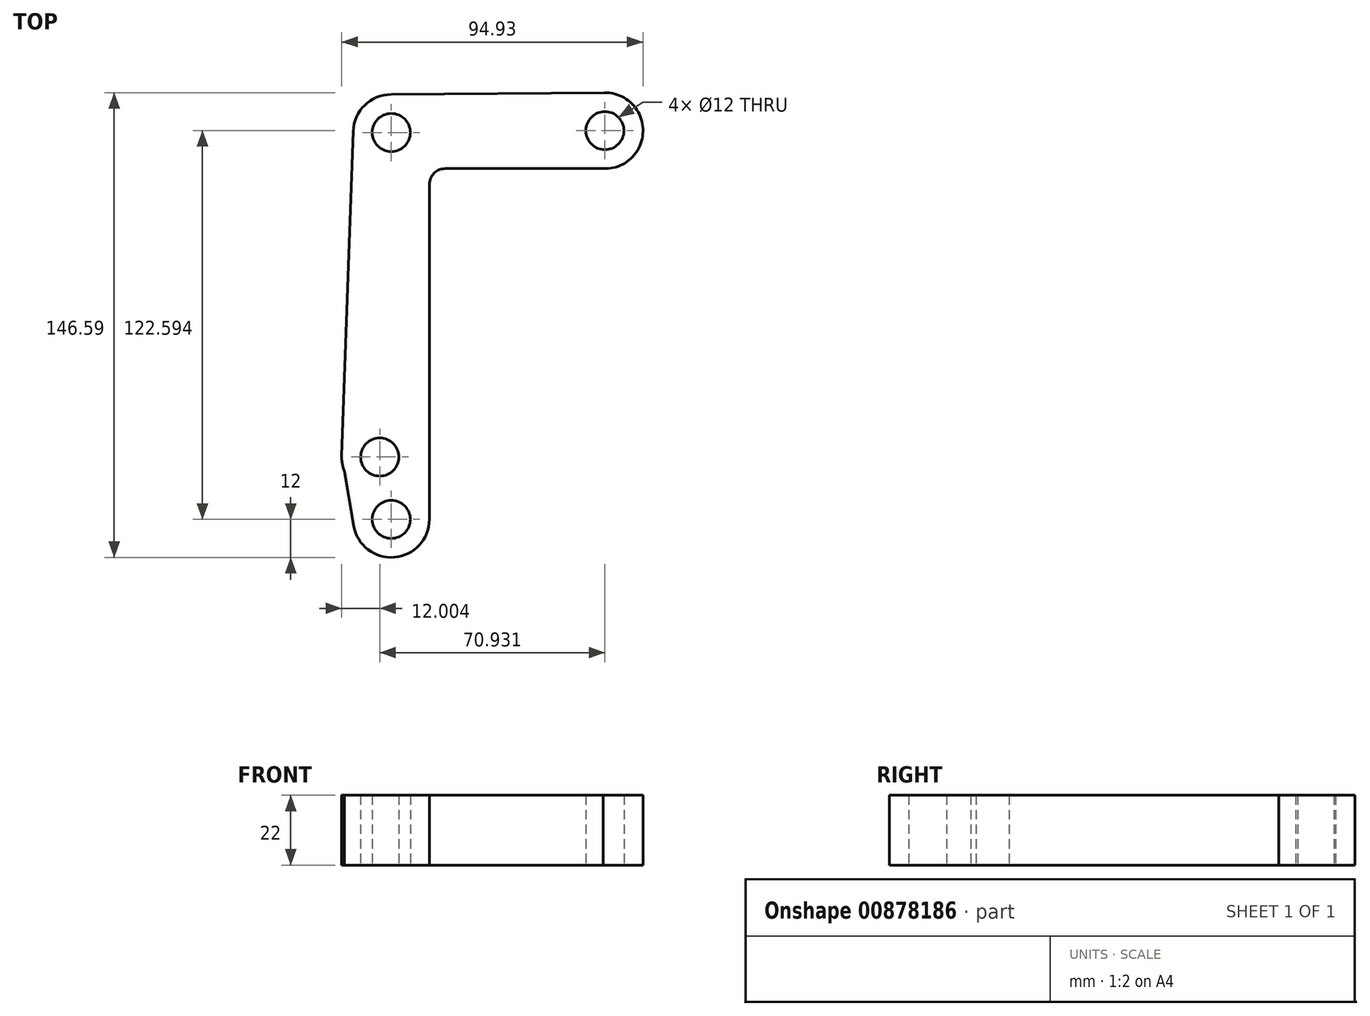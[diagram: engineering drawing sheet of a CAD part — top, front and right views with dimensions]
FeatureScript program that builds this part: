
annotation { "Feature Type Name" : "Feature", "Feature Type Description" : "" }
export const myFeature = defineFeature(function(context is Context, id is Id, definition is map)
    precondition{}
    {
        {
            var Q0;
            Q0=qCreatedBy(makeId("Top.planeOp"),FACE);
            var sketch = newSketch(context, id + "F0", { "sketchPlane" : qUnion([Q0])});
            skCircle(sketch, "E0", {"center": v(0, 0) * mm, "radius": 162 * mm, "construction": true});
            skLineSegment(sketch, "E1", {"start": v(-162, 0) * mm, "end": v(-116, 0) * mm, "construction": true});
            skLineSegment(sketch, "E2", {"start": v(-116, 0) * mm, "end": v(-70, 0) * mm, "construction": true});
            skLineSegment(sketch, "E3", {"start": v(-46.54, 61) * mm, "end": v(-46.54, -61) * mm, "construction": true});
            skCircle(sketch, "E4", {"center": v(0, 0) * mm, "radius": 65 * mm, "construction": true});
            skLineSegment(sketch, "E5", {"start": v(-50.17, -41.33) * mm, "end": v(20.76, 61.6) * mm, "construction": true});
            skCircle(sketch, "E6", {"center": v(20.76, 61.6) * mm, "radius": 6 * mm});
            skCircle(sketch, "E7", {"center": v(-50.17, -41.33) * mm, "radius": 6 * mm});
            skCircle(sketch, "E8", {"center": v(-46.54, -61) * mm, "radius": 6 * mm});
            skCircle(sketch, "E9", {"center": v(-46.54, 61) * mm, "radius": 6 * mm});
            skLineSegment(sketch, "E10", {"start": v(-46.54, -61) * mm, "end": v(-40.54, -61) * mm});
            skLineSegment(sketch, "E11.trimOffspring", {"start": v(-22.45, 61) * mm, "end": v(-22.34, 61) * mm});
            skArc(sketch, "E12.trimOffspring", {"start": v(-22.34, 61) * mm, "mid": v(-22.34, 61.02) * mm, "end": v(-22.34, 61.04) * mm});
            skCircle(sketch, "E13", {"center": v(20.76, 61.6) * mm, "radius": 12 * mm});
            skCircle(sketch, "E14", {"center": v(-46.54, 61) * mm, "radius": 12 * mm});
            skCircle(sketch, "E15", {"center": v(-46.54, -61) * mm, "radius": 12 * mm});
            skCircle(sketch, "E16", {"center": v(-50.17, -41.33) * mm, "radius": 12 * mm});
            skLineSegment(sketch, "E17", {"start": v(-58.53, 61.47) * mm, "end": v(-62.16, -40.9) * mm});
            skLineSegment(sketch, "E18", {"start": v(-62.16, -40.9) * mm, "end": v(-58.36, -63.03) * mm});
            skLineSegment(sketch, "E19", {"start": v(-46.75, 73) * mm, "end": v(20.66, 73.6) * mm});
            skLineSegment(sketch, "E20", {"start": v(20.76, 61.6) * mm, "end": v(20.66, 73.6) * mm});
            skLineSegment(sketch, "E21", {"start": v(20.76, 61.6) * mm, "end": v(20.76, 49.6) * mm});
            skLineSegment(sketch, "E22", {"start": v(-40.54, -61) * mm, "end": v(-34.54, -61) * mm});
            skLineSegment(sketch, "E23", {"start": v(-34.54, -61) * mm, "end": v(-34.54, 44.6) * mm});
            skLineSegment(sketch, "E24", {"start": v(20.76, 49.6) * mm, "end": v(-29.54, 49.6) * mm});
            skPoint(sketch, "E25.orphan", {"position": v(-34.54, 61) * mm});
            skPoint(sketch, "E26.visualSharp", {"position": v(-34.54, 49.6) * mm});
            skArc(sketch, "E26.filletArc", {"start": v(-29.54, 49.6) * mm, "mid": v(-33.07, 48.14) * mm, "end": v(-34.54, 44.6) * mm});
            skSolve(sketch);
        }
        {
            var Q0;
            Q0 = qSketchRegion(id + "F0", true);
            var Q1;
            {var subQ0=sQuery(id+"F0.wireOp",EDGE,"E16");var subQ1=sQuery(id+"F0.wireOp",EDGE,"E15");var subQ2=makeQuery(id+"F0.imprint","INTERSECT",VERTEX,{"disambiguationData":[OD(0.0)],"derivedFrom":[subQ1,subQ0]});Q1=makeQuery(id+"F0.imprint","IMPRINT",FACE,{"disambiguationData":[TD([[makeQuery(id+"F0.imprint","IMPRINT",EDGE,{"disambiguationData":[TD([[subQ2,-1.0]])],"derivedFrom":subQ1}),1.0]])]});}
            extrude(context, id + "F1", {"entities" : qUnion([Q0, Q1]), "depth" : 22 * mm, "offsetDistance" : 25 * mm});
        }
    });
